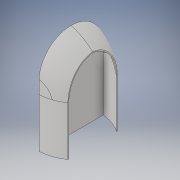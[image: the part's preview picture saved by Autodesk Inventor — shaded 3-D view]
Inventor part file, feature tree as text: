
AUTODESK INVENTOR PART (.ipt)
format: ipt  version: 2019 (Build 230136000, 136)  size: 325,632 bytes
history: native  units: mm
features: sketch x4, other x4, extrude x3, loft x2, shell x1, projected_geometry x1
ambient origin geometry x8: Origin, YZ Plane, XZ Plane, XY Plane, X Axis, Y Axis, Z Axis, Center Point
bodies: Body1 (feature_tree)
feature tree (15):
  sketch  "Эскиз4"
  other  "РабПлоскость1"
  sketch  "Эскиз5"
  loft  "Лофт1"
  extrude  "Выдавливание2"  Depth=100.0mm
  shell  "Оболочка1"  Thickness=17.0mm
  other  "РабПлоскость2"
  other  "РабПлоскость6"
  extrude  "Выдавливание7"  Depth=4.0mm
  other  "РабПлоскость5"
  loft  "Лофт2"
  extrude  "Выдавливание13"  TaperAngle=0.0deg  [1 undecoded]
  sketch  "Эскиз6"
  projected_geometry  "Спроецированная петля1"
  sketch  "Эскиз19"
note: 1 required parameter value undecoded (feature->parameter linkage not recoverable at this tier; creation-order binding heuristic only, values carry confidence <= 0.55)
